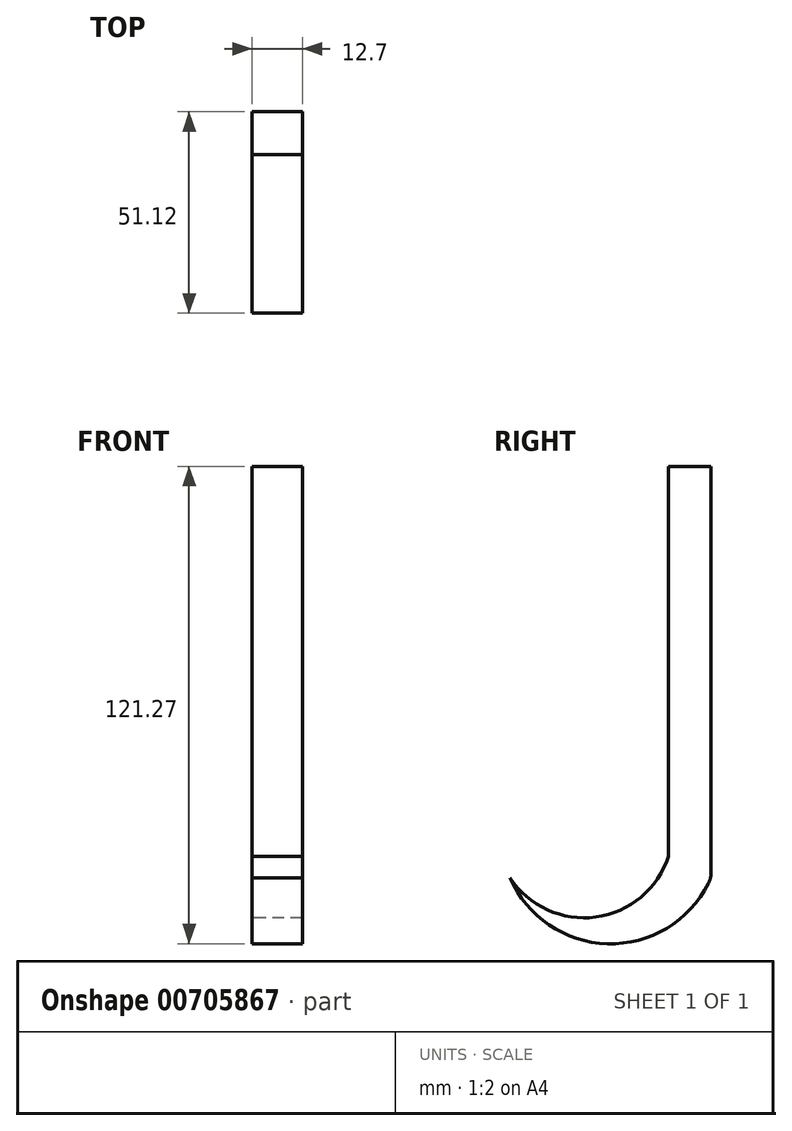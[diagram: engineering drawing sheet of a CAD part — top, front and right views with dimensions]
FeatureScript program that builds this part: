
annotation { "Feature Type Name" : "Feature", "Feature Type Description" : "" }
export const myFeature = defineFeature(function(context is Context, id is Id, definition is map)
    precondition{}
    {
        {
            var Q0;
            Q0=qCreatedBy(makeId("Right.planeOp"),FACE);
            var sketch = newSketch(context, id + "F0", { "sketchPlane" : qUnion([Q0])});
            skLineSegment(sketch, "E0", {"start": v(-18.77, 60.84) * mm, "end": v(-18.77, -42.24) * mm});
            skArc(sketch, "E1", {"start": v(-69.89, -43.65) * mm, "mid": v(-45.13, -60.42) * mm, "end": v(-19.45, -45.1) * mm});
            skLineSegment(sketch, "E2", {"start": v(-18.77, 60.84) * mm, "end": v(-29.63, 60.84) * mm});
            skLineSegment(sketch, "E3", {"start": v(-29.63, 60.84) * mm, "end": v(-29.63, -38.22) * mm});
            skArc(sketch, "E4", {"start": v(-69.89, -43.65) * mm, "mid": v(-48.04, -53.63) * mm, "end": v(-29.63, -38.22) * mm});
            skPoint(sketch, "E5.visualSharp", {"position": v(-18.77, -43.65) * mm});
            skArc(sketch, "E5.filletArc", {"start": v(-19.45, -45.1) * mm, "mid": v(-18.94, -43.71) * mm, "end": v(-18.77, -42.24) * mm});
            skSolve(sketch);
        }
        {
            var Q0;
            Q0=makeQuery(id+"F0.imprint","IMPRINT",FACE,{"disambiguationData":[TD([[makeQuery(id+"F0.imprint","IMPRINT",EDGE,{"derivedFrom":sQuery(id+"F0.wireOp",EDGE,"E0")}),-1.0]])]});
            extrude(context, id + "F1", {"entities" : qUnion([Q0]), "depth" : 12.7 * mm, "offsetDistance" : 25.4 * mm});
        }
    });
